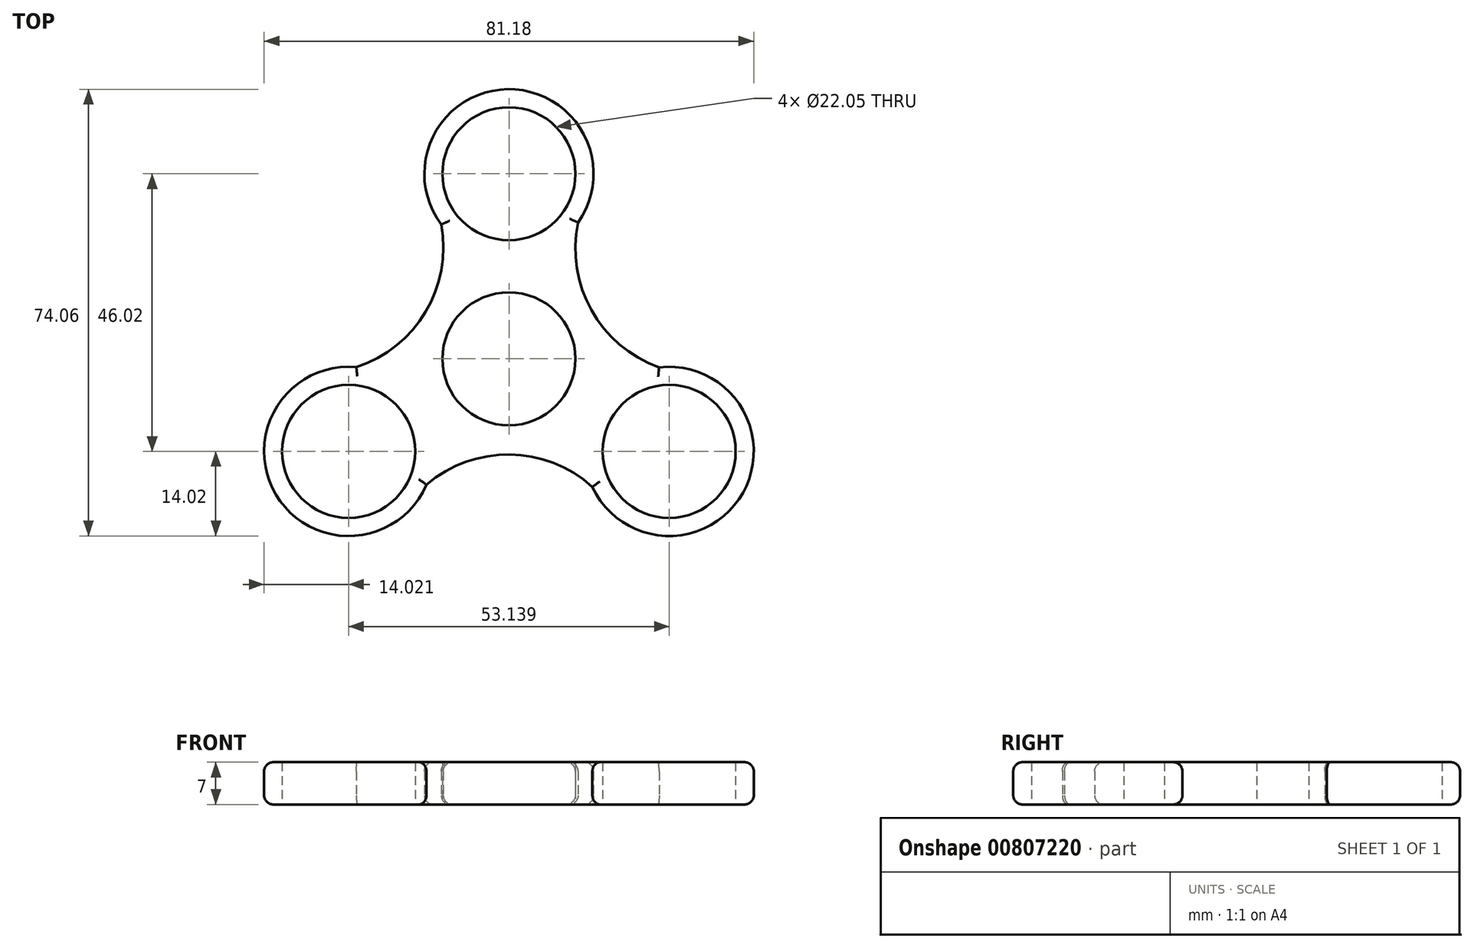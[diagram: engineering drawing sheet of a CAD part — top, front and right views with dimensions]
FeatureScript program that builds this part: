
annotation { "Feature Type Name" : "Feature", "Feature Type Description" : "" }
export const myFeature = defineFeature(function(context is Context, id is Id, definition is map)
    precondition{}
    {
        {
            var Q0;
            Q0=qCreatedBy(makeId("Top.planeOp"),FACE);
            var sketch = newSketch(context, id + "F0", { "sketchPlane" : qUnion([Q0])});
            skCircle(sketch, "E0", {"center": v(0, 0) * mm, "radius": 11.03 * mm});
            skCircle(sketch, "E1", {"center": v(0, 30.68) * mm, "radius": 11.03 * mm});
            skArc(sketch, "E2", {"start": v(11.46, 22.6) * mm, "mid": v(-0.2, 44.7) * mm, "end": v(-11.23, 22.28) * mm});
            skCircle(sketch, "E3.1.0", {"center": v(-26.57, -15.34) * mm, "radius": 11.03 * mm});
            skArc(sketch, "E3.1.1", {"start": v(-25.3, -1.37) * mm, "mid": v(-38.61, -22.52) * mm, "end": v(-13.68, -20.86) * mm});
            skCircle(sketch, "E3.2.0", {"center": v(26.57, -15.34) * mm, "radius": 11.03 * mm});
            skArc(sketch, "E3.2.1", {"start": v(13.84, -21.23) * mm, "mid": v(38.81, -22.18) * mm, "end": v(24.9, -1.41) * mm});
            skLineSegment(sketch, "E4", {"start": v(0, 30.68) * mm, "end": v(5.51, 21.13) * mm, "construction": true});
            skArc(sketch, "E5", {"start": v(11.46, 22.6) * mm, "mid": v(13.67, 8.07) * mm, "end": v(24.9, -1.41) * mm});
            skArc(sketch, "E6.1.0", {"start": v(-25.3, -1.37) * mm, "mid": v(-13.82, 7.8) * mm, "end": v(-11.23, 22.28) * mm});
            skArc(sketch, "E6.2.0", {"start": v(13.84, -21.23) * mm, "mid": v(0.15, -15.88) * mm, "end": v(-13.68, -20.86) * mm});
            skSolve(sketch);
        }
        {
            var Q0;
            Q0=makeQuery(id+"F0.imprint","IMPRINT",FACE,{"disambiguationData":[TD([[makeQuery(id+"F0.imprint","IMPRINT",EDGE,{"derivedFrom":sQuery(id+"F0.wireOp",EDGE,"E0")}),-1.0]])]});
            extrude(context, id + "F1", {"entities" : qUnion([Q0]), "depth" : 7 * mm, "offsetDistance" : 25 * mm});
        }
        {
            var Q0;
            Q0=makeQuery(id+"F1.opExtrude","CAP_EDGE",EDGE,{"disambiguationData":[OSD([sQuery(id+"F0.wireOp",EDGE,"E6.2.0")])],"isStart":false});
            var Q1;
            Q1=makeQuery(id+"F1.opExtrude","CAP_EDGE",EDGE,{"disambiguationData":[OSD([sQuery(id+"F0.wireOp",EDGE,"E3.1.1")])],"isStart":false});
            var Q2;
            Q2=makeQuery(id+"F1.opExtrude","CAP_EDGE",EDGE,{"disambiguationData":[OSD([sQuery(id+"F0.wireOp",EDGE,"E6.1.0")])],"isStart":false});
            var Q3;
            Q3=makeQuery(id+"F1.opExtrude","CAP_EDGE",EDGE,{"disambiguationData":[OSD([sQuery(id+"F0.wireOp",EDGE,"E2")])],"isStart":false});
            var Q4;
            Q4=makeQuery(id+"F1.opExtrude","CAP_EDGE",EDGE,{"disambiguationData":[OSD([sQuery(id+"F0.wireOp",EDGE,"E5")])],"isStart":false});
            var Q5;
            Q5=makeQuery(id+"F1.opExtrude","CAP_EDGE",EDGE,{"disambiguationData":[OSD([sQuery(id+"F0.wireOp",EDGE,"E3.2.1")])],"isStart":false});
            var Q6;
            Q6=makeQuery(id+"F1.opExtrude","CAP_EDGE",EDGE,{"disambiguationData":[OSD([sQuery(id+"F0.wireOp",EDGE,"E6.2.0")])],"isStart":true});
            var Q7;
            Q7=makeQuery(id+"F1.opExtrude","CAP_EDGE",EDGE,{"disambiguationData":[OSD([sQuery(id+"F0.wireOp",EDGE,"E3.1.1")])],"isStart":true});
            var Q8;
            Q8=makeQuery(id+"F1.opExtrude","CAP_EDGE",EDGE,{"disambiguationData":[OSD([sQuery(id+"F0.wireOp",EDGE,"E6.1.0")])],"isStart":true});
            var Q9;
            Q9=makeQuery(id+"F1.opExtrude","CAP_EDGE",EDGE,{"disambiguationData":[OSD([sQuery(id+"F0.wireOp",EDGE,"E2")])],"isStart":true});
            var Q10;
            Q10=makeQuery(id+"F1.opExtrude","CAP_EDGE",EDGE,{"disambiguationData":[OSD([sQuery(id+"F0.wireOp",EDGE,"E5")])],"isStart":true});
            var Q11;
            Q11=makeQuery(id+"F1.opExtrude","CAP_EDGE",EDGE,{"disambiguationData":[OSD([sQuery(id+"F0.wireOp",EDGE,"E3.2.1")])],"isStart":true});
            fillet(context, id + "F2", {"entities" : qUnion([Q0, Q1, Q2, Q3, Q4, Q5, Q6, Q7, Q8, Q9, Q10, Q11]), "radius" : 1.5 * mm, "tangentPropagation" : true, "allowEdgeOverflow" : false});
        }
    });
